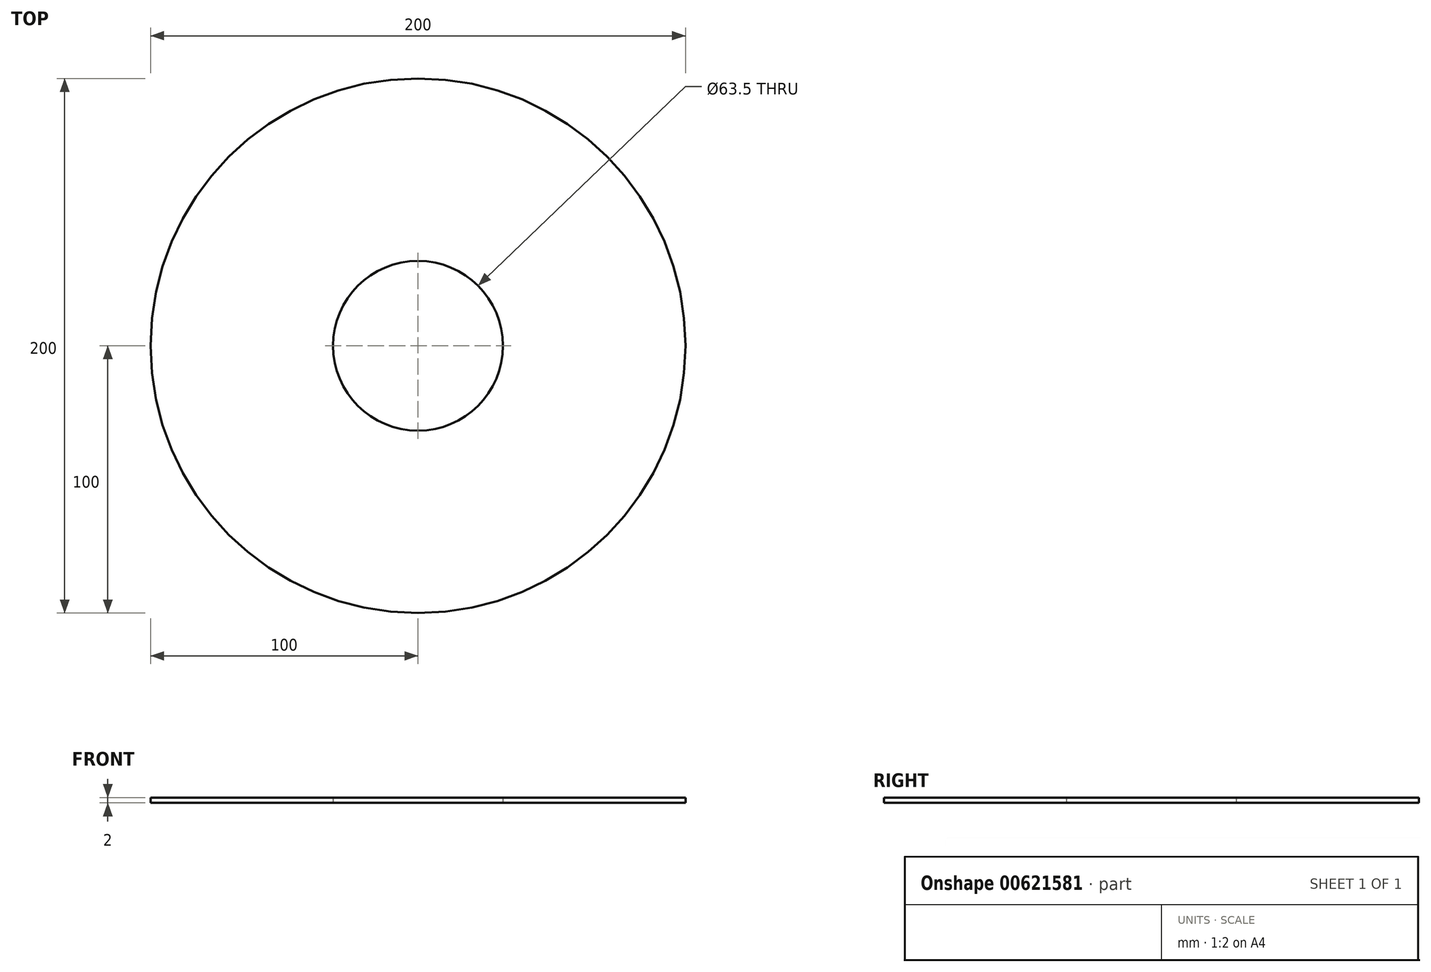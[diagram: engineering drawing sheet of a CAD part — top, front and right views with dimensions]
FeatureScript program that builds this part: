
annotation { "Feature Type Name" : "Feature", "Feature Type Description" : "" }
export const myFeature = defineFeature(function(context is Context, id is Id, definition is map)
    precondition{}
    {
        {
            var Q0;
            Q0=qCreatedBy(makeId("Top.planeOp"),FACE);
            var sketch = newSketch(context, id + "F0", { "sketchPlane" : qUnion([Q0])});
            skCircle(sketch, "E0", {"center": v(0, 0) * mm, "radius": 31.75 * mm});
            skCircle(sketch, "E1", {"center": v(0, 0) * mm, "radius": 100 * mm});
            skSolve(sketch);
        }
        {
            var Q0;
            Q0 = qSketchRegion(id + "F0", true);
            extrude(context, id + "F1", {"entities" : qUnion([Q0]), "depth" : 2 * mm, "offsetDistance" : 25 * mm});
        }
    });
